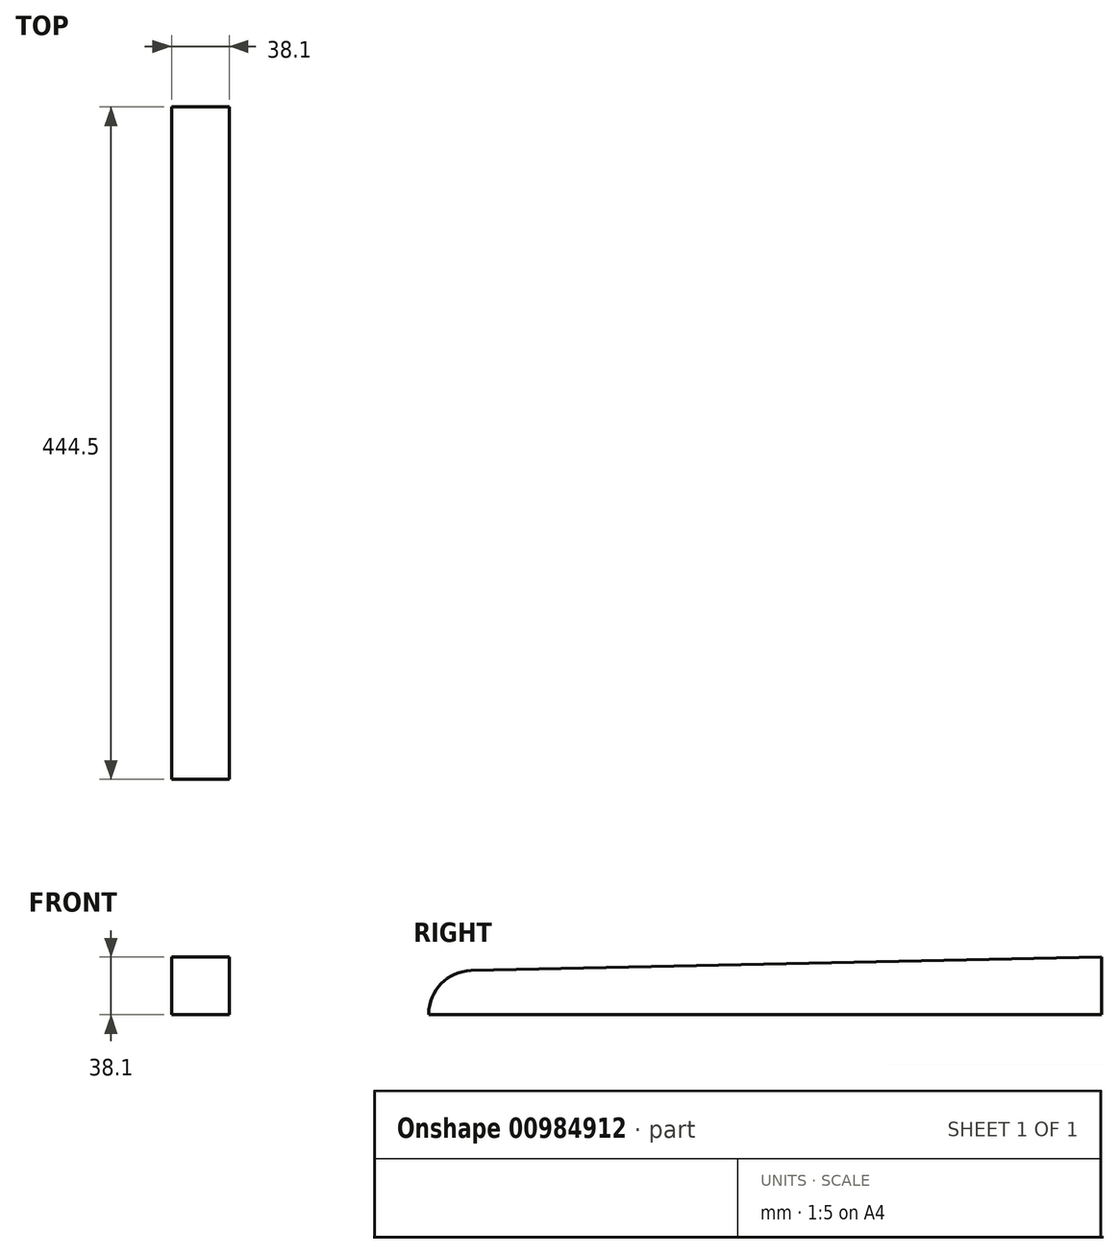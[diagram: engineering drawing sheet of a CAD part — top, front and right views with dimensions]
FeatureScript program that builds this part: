
annotation { "Feature Type Name" : "Feature", "Feature Type Description" : "" }
export const myFeature = defineFeature(function(context is Context, id is Id, definition is map)
    precondition{}
    {
        {
            var Q0;
            Q0=qCreatedBy(makeId("Right.planeOp"),FACE);
            var sketch = newSketch(context, id + "F0", { "sketchPlane" : qUnion([Q0])});
            skLineSegment(sketch, "E0.bottom", {"start": v(0, 0) * mm, "end": v(-444.5, 0) * mm});
            skLineSegment(sketch, "E0.left", {"start": v(0, 0) * mm, "end": v(0, 38.1) * mm});
            skLineSegment(sketch, "E1", {"start": v(-444.5, 0) * mm, "end": v(-444.5, 0.6) * mm});
            skLineSegment(sketch, "E2", {"start": v(-416.54, 29.17) * mm, "end": v(0, 38.1) * mm});
            skPoint(sketch, "E3.visualSharp", {"position": v(-444.5, 28.58) * mm});
            skArc(sketch, "E3.filletArc", {"start": v(-416.54, 29.17) * mm, "mid": v(-436.35, 20.6) * mm, "end": v(-444.5, 0.6) * mm});
            skSolve(sketch);
        }
        {
            var Q0;
            Q0 = qSketchRegion(id + "F0", true);
            extrude(context, id + "F1", {"entities" : qUnion([Q0]), "depth" : 38.1 * mm, "offsetDistance" : 25.4 * mm});
        }
    });
